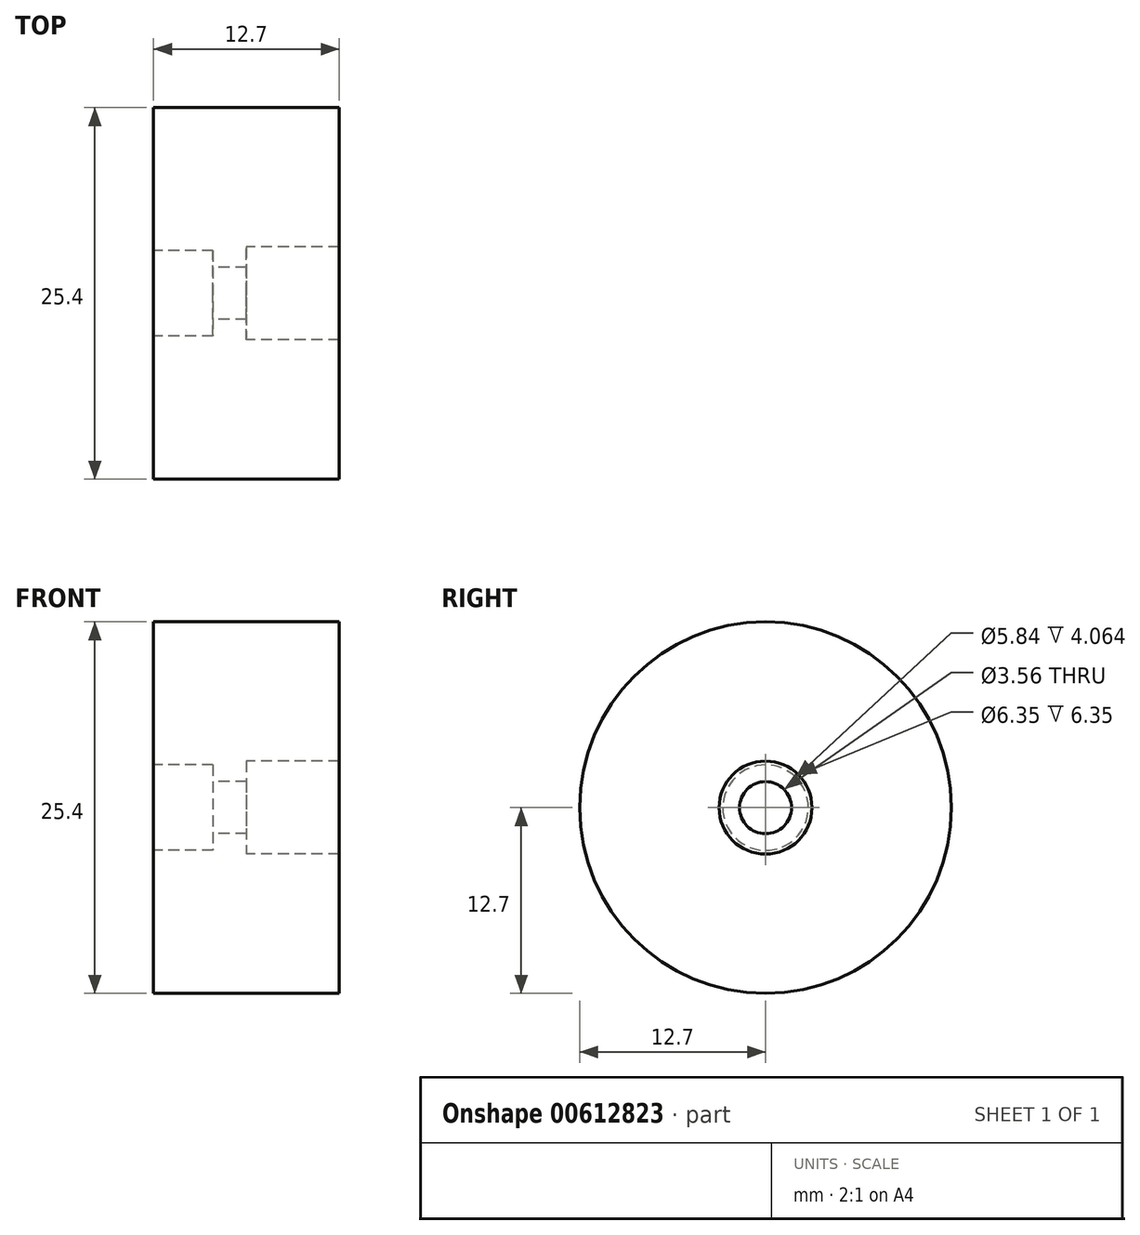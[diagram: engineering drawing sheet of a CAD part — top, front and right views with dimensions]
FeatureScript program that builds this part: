
annotation { "Feature Type Name" : "Feature", "Feature Type Description" : "" }
export const myFeature = defineFeature(function(context is Context, id is Id, definition is map)
    precondition{}
    {
        {
            var Q0;
            Q0=qCreatedBy(makeId("Front.planeOp"),FACE);
            var sketch = newSketch(context, id + "F0", { "sketchPlane" : qUnion([Q0])});
            skLineSegment(sketch, "E0", {"start": v(-44.24, 0) * mm, "end": v(42.95, 0) * mm, "construction": true});
            skLineSegment(sketch, "E1", {"start": v(-6.35, 2.92) * mm, "end": v(-6.35, 12.7) * mm});
            skLineSegment(sketch, "E2", {"start": v(-6.35, 12.7) * mm, "end": v(6.35, 12.7) * mm});
            skLineSegment(sketch, "E3", {"start": v(6.35, 12.7) * mm, "end": v(6.35, 3.17) * mm});
            skLineSegment(sketch, "E4", {"start": v(6.35, 3.18) * mm, "end": v(0, 3.17) * mm});
            skLineSegment(sketch, "E5", {"start": v(0, 3.17) * mm, "end": v(0, 1.78) * mm});
            skLineSegment(sketch, "E6", {"start": v(0, 1.78) * mm, "end": v(-2.29, 1.78) * mm});
            skLineSegment(sketch, "E7", {"start": v(-2.29, 1.78) * mm, "end": v(-2.29, 2.92) * mm});
            skLineSegment(sketch, "E8", {"start": v(-2.29, 2.92) * mm, "end": v(-6.35, 2.92) * mm});
            skPoint(sketch, "E9", {"position": v(0, 12.7) * mm});
            skSolve(sketch);
        }
        {
            var Q0;
            Q0=qSketchRegion(id+"F0",true);
            var Q1;
            Q1=sQuery(id+"F0.wireOp",EDGE,"E0");
            revolve(context, id + "F1", {"entities" : qUnion([Q0]), "axis" : qUnion([Q1]), "revolveType" : RevolveType.FULL});
        }
    });
